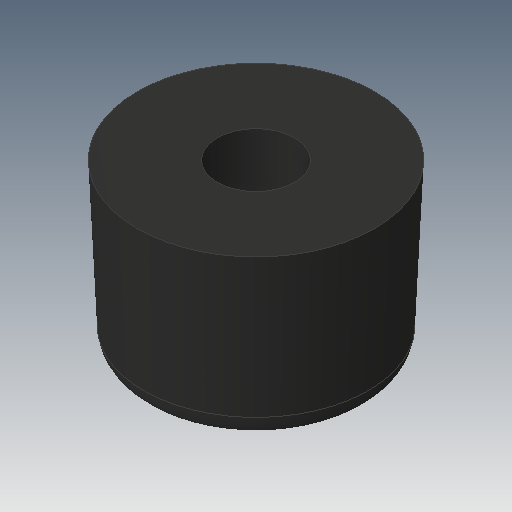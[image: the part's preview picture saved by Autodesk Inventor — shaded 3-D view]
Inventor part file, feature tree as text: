
AUTODESK INVENTOR PART (.ipt)
format: ipt  version: 2017 (Build 210142000, 142)  size: 114,176 bytes
history: native  units: in
note: dims shown in document units (in); Inventor stores cm internally (conversion verified against a paired STEP export)
features: sketch x2, extrude x1, hole x1, draft x1, fillet x1
ambient origin geometry x8: Origin, YZ Plane, XZ Plane, XY Plane, X Axis, Y Axis, Z Axis, Center Point
bodies: Solid1 (feature_tree)
feature tree (6):
  extrude  "Extrusion1"  Depth=0.4375in TaperAngle=0.0deg
  hole  "Hole1"  [1 undecoded]
  draft  "FaceDraft1"
  fillet  "Fillet1"  Radius=0.0625in
  sketch  "Sketch1"  dims[d0=0.625in d1=0.4375in d2=0.0in]
  sketch  "Sketch2"  dims[d3=0.2031in d4=0.75in d5=0.3125in d6=0.25in d7=0.5635in d8=1.0in d9=0.8108in d10=0.0172in d11=0.0625in]
note: 1 required parameter value undecoded (feature->parameter linkage not recoverable at this tier; creation-order binding heuristic only, values carry confidence <= 0.55)
